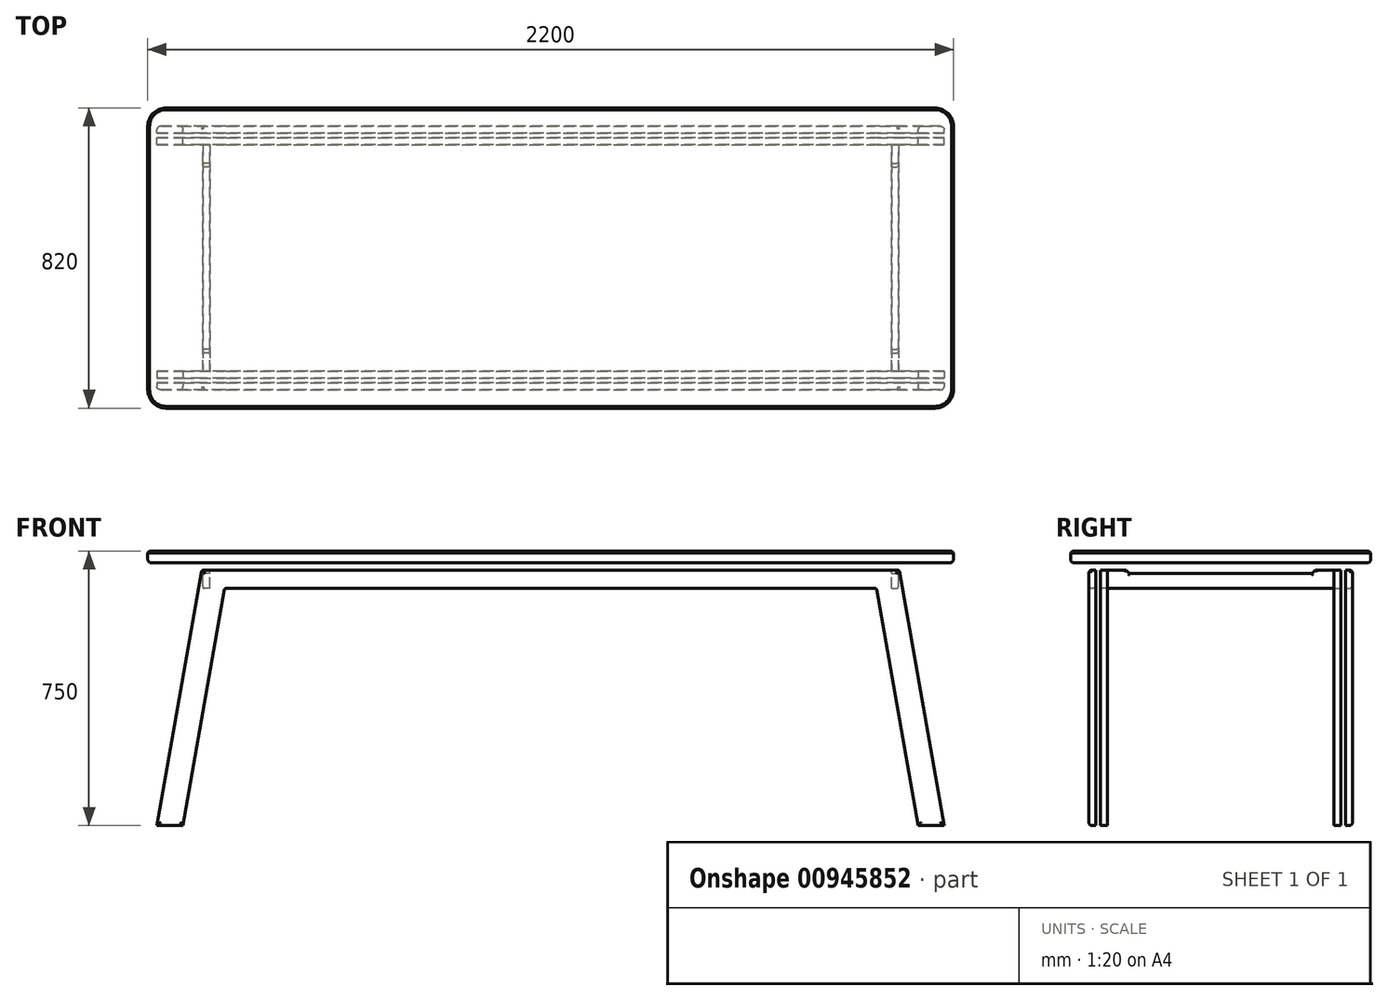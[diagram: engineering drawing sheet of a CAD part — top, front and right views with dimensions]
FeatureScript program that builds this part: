
annotation { "Feature Type Name" : "Feature", "Feature Type Description" : "" }
export const myFeature = defineFeature(function(context is Context, id is Id, definition is map)
    precondition{}
    {
        {
            assignVariable(context, id + "F0", {"name" : "chama", "anyValue" : 5});
        }
        {
            assignVariable(context, id + "F1", {"name" : "fila", "anyValue" : 50});
        }
        {
            assignVariable(context, id + "F2", {"name" : "filb", "anyValue" : 9});
        }
        {
            assignVariable(context, id + "F3", {"name" : "filc", "anyValue" : 5});
        }
        {
            assignVariable(context, id + "F4", {"name" : "w", "anyValue" : 820});
        }
        {
            assignVariable(context, id + "F5", {"name" : "h", "anyValue" : 750});
        }
        {
            assignVariable(context, id + "F6", {"name" : "ld", "anyValue" : 19});
        }
        {
            assignVariable(context, id + "F7", {"name" : "thk", "anyValue" : 32});
        }
        {
            var Q0;
            Q0=qCreatedBy(makeId("Right.planeOp"),FACE);
            cPlane(context, id + "F8", {"entities" : qUnion([Q0]), "cplaneType" : CPlaneType.OFFSET, "offset" : 950 * mm, "width" : 150 * mm, "height" : 150 * mm});
        }
        {
            var Q0;
            Q0=qCreatedBy(makeId("Front.planeOp"),FACE);
            cPlane(context, id + "F9", {"entities" : qUnion([Q0]), "cplaneType" : CPlaneType.OFFSET, "offset" : (getVariable(context, 'w') / 2 - 50) * mm, "width" : 150 * mm, "height" : 150 * mm});
        }
        {
            var Q0;
            Q0=qCreatedBy(makeId("Top.planeOp"),FACE);
            var sketch = newSketch(context, id + "F10", { "sketchPlane" : qUnion([Q0])});
            skLineSegment(sketch, "E0.bottom", {"start": v(1100, -410) * mm, "end": v(-1100, -410) * mm});
            skLineSegment(sketch, "E0.top", {"start": v(1100, 410) * mm, "end": v(-1100, 410) * mm});
            skLineSegment(sketch, "E0.left", {"start": v(1100, -410) * mm, "end": v(1100, 410) * mm});
            skLineSegment(sketch, "E0.right", {"start": v(-1100, -410) * mm, "end": v(-1100, 410) * mm});
            skPoint(sketch, "E0.middle", {"position": v(0, 0) * mm});
            skSolve(sketch);
        }
        {
            var Q0;
            Q0=sQuery(id+"F10.wireOp",EDGE,"E0.top");
            var Q1;
            Q1=sQuery(id+"F10.wireOp",EDGE,"E0.right");
            var Q2;
            Q2=sQuery(id+"F10.wireOp",EDGE,"E0.bottom");
            var Q3;
            Q3=sQuery(id+"F10.wireOp",EDGE,"E0.left");
            extrude(context, id + "F11", {"bodyType" : ToolBodyType.SURFACE, "surfaceEntities" : qUnion([Q0, Q1, Q2, Q3]), "oppositeDirection" : true, "depth" : (getVariable(context, 'h')) * mm, "offsetDistance" : 25.4 * mm});
        }
        {
            var Q0;
            Q0=makeQuery(id+"F10.imprint","IMPRINT",FACE,{"disambiguationData":[TD([[makeQuery(id+"F10.imprint","IMPRINT",EDGE,{"derivedFrom":sQuery(id+"F10.wireOp",EDGE,"E0.bottom")}),-1.0]])]});
            extrude(context, id + "F12", {"entities" : qUnion([Q0]), "oppositeDirection" : true, "depth" : (getVariable(context, 'thk')) * mm, "offsetDistance" : 25.4 * mm});
        }
        {
            var Q0;
            Q0=qCreatedBy(id+"F9.planeOp",FACE);
            var sketch = newSketch(context, id + "F13", { "sketchPlane" : qUnion([Q0])});
            skLineSegment(sketch, "E1", {"start": v(1075, -750) * mm, "end": v(951.92, -52) * mm});
            skLineSegment(sketch, "E2", {"start": v(951.92, -52) * mm, "end": v(-951.92, -52) * mm});
            skLineSegment(sketch, "E3", {"start": v(-951.92, -52) * mm, "end": v(-1075, -750) * mm});
            skLineSegment(sketch, "E4", {"start": v(-1075, -750) * mm, "end": v(-1003.92, -750) * mm});
            skLineSegment(sketch, "E5", {"start": v(-1003.92, -750) * mm, "end": v(-889.66, -102) * mm});
            skLineSegment(sketch, "E6", {"start": v(-889.66, -102) * mm, "end": v(889.66, -102) * mm});
            skLineSegment(sketch, "E7", {"start": v(889.66, -102) * mm, "end": v(1003.92, -750) * mm});
            skLineSegment(sketch, "E8", {"start": v(1003.92, -750) * mm, "end": v(1075, -750) * mm});
            skSolve(sketch);
        }
        {
            var Q0;
            Q0 = qSketchRegion(id + "F13", true);
            extrude(context, id + "F14", {"entities" : qUnion([Q0]), "oppositeDirection" : true, "depth" : (getVariable(context, 'ld')) * mm, "offsetDistance" : 25 * mm});
        }
        {
            var Q0;
            Q0=makeQuery(id+"F12.opExtrude","SWEPT_EDGE",EDGE,{"disambiguationData":[OSD([sQuery(id+"F10.wireOp",EDGE,"E0.bottom"),sQuery(id+"F10.wireOp",EDGE,"E0.left")])]});
            var Q1;
            Q1=makeQuery(id+"F12.opExtrude","SWEPT_EDGE",EDGE,{"disambiguationData":[OSD([sQuery(id+"F10.wireOp",EDGE,"E0.top"),sQuery(id+"F10.wireOp",EDGE,"E0.left")])]});
            var Q2;
            Q2=makeQuery(id+"F12.opExtrude","SWEPT_EDGE",EDGE,{"disambiguationData":[OSD([sQuery(id+"F10.wireOp",EDGE,"E0.top"),sQuery(id+"F10.wireOp",EDGE,"E0.right")])]});
            var Q3;
            Q3=makeQuery(id+"F12.opExtrude","SWEPT_EDGE",EDGE,{"disambiguationData":[OSD([sQuery(id+"F10.wireOp",EDGE,"E0.bottom"),sQuery(id+"F10.wireOp",EDGE,"E0.right")])]});
            fillet(context, id + "F15", {"entities" : qUnion([Q0, Q1, Q2, Q3]), "radius" : (getVariable(context, 'fila')) * mm, "tangentPropagation" : true, "allowEdgeOverflow" : false});
        }
        {
            var Q0;
            Q0=makeQuery(id+"F12.opExtrude","CAP_FACE",FACE,{"disambiguationData":[OSD([sQuery(id+"F10.wireOp",EDGE,"E0.bottom"),sQuery(id+"F10.wireOp",EDGE,"E0.top"),sQuery(id+"F10.wireOp",EDGE,"E0.left"),sQuery(id+"F10.wireOp",EDGE,"E0.right")])],"isStart":false});
            fillet(context, id + "F16", {"entities" : qUnion([Q0]), "radius" : (getVariable(context, 'filb')) * mm, "tangentPropagation" : true, "allowEdgeOverflow" : false});
        }
        {
            var Q0;
            Q0=makeQuery(id+"F12.opExtrude","CAP_FACE",FACE,{"disambiguationData":[OSD([sQuery(id+"F10.wireOp",EDGE,"E0.bottom"),sQuery(id+"F10.wireOp",EDGE,"E0.top"),sQuery(id+"F10.wireOp",EDGE,"E0.left"),sQuery(id+"F10.wireOp",EDGE,"E0.right")])],"isStart":true});
            chamfer(context, id + "F17", {"entities" : qUnion([Q0]), "width" : (getVariable(context, 'chama')) * mm, "tangentPropagation" : true});
        }
        {
            var Q0;
            Q0=makeQuery(id+"F14.opExtrude","SWEPT_EDGE",EDGE,{"disambiguationData":[OSD([sQuery(id+"F13.wireOp",EDGE,"E1"),sQuery(id+"F13.wireOp",EDGE,"E2")])]});
            var Q1;
            Q1=makeQuery(id+"F14.opExtrude","SWEPT_EDGE",EDGE,{"disambiguationData":[OSD([sQuery(id+"F13.wireOp",EDGE,"E2"),sQuery(id+"F13.wireOp",EDGE,"E3")])]});
            var Q2;
            Q2=makeQuery(id+"F14.opExtrude","SWEPT_EDGE",EDGE,{"disambiguationData":[OSD([sQuery(id+"F13.wireOp",EDGE,"E6"),sQuery(id+"F13.wireOp",EDGE,"E7")])]});
            var Q3;
            Q3=makeQuery(id+"F14.opExtrude","SWEPT_EDGE",EDGE,{"disambiguationData":[OSD([sQuery(id+"F13.wireOp",EDGE,"E5"),sQuery(id+"F13.wireOp",EDGE,"E6")])]});
            fillet(context, id + "F18", {"entities" : qUnion([Q0, Q1, Q2, Q3]), "radius" : (getVariable(context, 'filc')) * mm, "tangentPropagation" : true, "allowEdgeOverflow" : false});
        }
        {
            var Q0;
            Q0=makeQuery(id+"F14.opExtrude","SWEPT_BODY",BODY,{"disambiguationData":[OSD([sQuery(id+"F13.wireOp",EDGE,"E1"),sQuery(id+"F13.wireOp",EDGE,"E2"),sQuery(id+"F13.wireOp",EDGE,"E3"),sQuery(id+"F13.wireOp",EDGE,"E4"),sQuery(id+"F13.wireOp",EDGE,"E5"),sQuery(id+"F13.wireOp",EDGE,"E6"),sQuery(id+"F13.wireOp",EDGE,"E7"),sQuery(id+"F13.wireOp",EDGE,"E8")])]});
            transform(context, id + "F19", {"entities" : qUnion([Q0]), "transformType" : TransformType.TRANSLATION_3D, "dx" : 0 * mm, "dy" : (getVariable(context, 'thk')) * mm, "dz" : 0 * mm, "makeCopy" : true});
        }
        {
            var Q0;
            Q0=makeQuery(id+"F14.opExtrude","CAP_FACE",FACE,{"disambiguationData":[OSD([sQuery(id+"F13.wireOp",EDGE,"E1"),sQuery(id+"F13.wireOp",EDGE,"E2"),sQuery(id+"F13.wireOp",EDGE,"E3"),sQuery(id+"F13.wireOp",EDGE,"E4"),sQuery(id+"F13.wireOp",EDGE,"E5"),sQuery(id+"F13.wireOp",EDGE,"E6"),sQuery(id+"F13.wireOp",EDGE,"E7"),sQuery(id+"F13.wireOp",EDGE,"E8")])],"isStart":true});
            fillet(context, id + "F20", {"entities" : qUnion([Q0]), "radius" : (getVariable(context, 'filb')) * mm, "tangentPropagation" : true, "allowEdgeOverflow" : false});
        }
        {
            var Q0;
            Q0=makeQuery(id+"F14.opExtrude","SWEPT_BODY",BODY,{"disambiguationData":[OSD([sQuery(id+"F13.wireOp",EDGE,"E1"),sQuery(id+"F13.wireOp",EDGE,"E2"),sQuery(id+"F13.wireOp",EDGE,"E3"),sQuery(id+"F13.wireOp",EDGE,"E4"),sQuery(id+"F13.wireOp",EDGE,"E5"),sQuery(id+"F13.wireOp",EDGE,"E6"),sQuery(id+"F13.wireOp",EDGE,"E7"),sQuery(id+"F13.wireOp",EDGE,"E8")])]});
            var Q1;
            Q1=makeQuery(id+"F19.opPattern","COPY",BODY,{"derivedFrom":makeQuery(id+"F14.opExtrude","SWEPT_BODY",BODY,{"disambiguationData":[OSD([sQuery(id+"F13.wireOp",EDGE,"E1"),sQuery(id+"F13.wireOp",EDGE,"E2"),sQuery(id+"F13.wireOp",EDGE,"E3"),sQuery(id+"F13.wireOp",EDGE,"E4"),sQuery(id+"F13.wireOp",EDGE,"E5"),sQuery(id+"F13.wireOp",EDGE,"E6"),sQuery(id+"F13.wireOp",EDGE,"E7"),sQuery(id+"F13.wireOp",EDGE,"E8")])]}),"instanceName":"1"});
            var Q2;
            Q2=qCreatedBy(makeId("Front.planeOp"),FACE);
            mirror(context, id + "F21", {"entities" : qUnion([Q0, Q1]), "mirrorPlane" : qUnion([Q2])});
        }
        {
            var Q0;
            Q0=qCreatedBy(id+"F8.planeOp",FACE);
            var sketch = newSketch(context, id + "F22", { "sketchPlane" : qUnion([Q0])});
            skLineSegment(sketch, "E9", {"start": v(-309, -52) * mm, "end": v(309, -52) * mm});
            skLineSegment(sketch, "E10", {"start": v(309, -52) * mm, "end": v(309, -102) * mm});
            skLineSegment(sketch, "E11", {"start": v(309, -102) * mm, "end": v(-309, -102) * mm});
            skLineSegment(sketch, "E12", {"start": v(-309, -102) * mm, "end": v(-309, -52) * mm});
            skLineSegment(sketch, "E13", {"start": v(-259, -52) * mm, "end": v(-249, -62) * mm});
            skLineSegment(sketch, "E14", {"start": v(-249, -62) * mm, "end": v(249, -62) * mm});
            skLineSegment(sketch, "E15", {"start": v(249, -62) * mm, "end": v(259, -52) * mm});
            skSolve(sketch);
        }
        {
            var Q0;
            Q0=makeQuery(id+"F22.imprint","IMPRINT",FACE,{"disambiguationData":[TD([[makeQuery(id+"F22.imprint","IMPRINT",EDGE,{"derivedFrom":sQuery(id+"F22.wireOp",EDGE,"E9")}),-1.0]])]});
            extrude(context, id + "F23", {"entities" : qUnion([Q0]), "oppositeDirection" : true, "depth" : (getVariable(context, 'ld')) * mm, "offsetDistance" : 25 * mm});
        }
        {
            var Q0;
            Q0=makeQuery(id+"F23.opExtrude","CAP_EDGE",EDGE,{"disambiguationData":[OSD([sQuery(id+"F22.wireOp",EDGE,"E9")])],"isStart":true});
            var Q1;
            Q1=makeQuery(id+"F23.opExtrude","CAP_EDGE",EDGE,{"disambiguationData":[OSD([sQuery(id+"F22.wireOp",EDGE,"E11")])],"isStart":true});
            var Q2;
            Q2=makeQuery(id+"F23.opExtrude","CAP_EDGE",EDGE,{"disambiguationData":[OSD([sQuery(id+"F22.wireOp",EDGE,"E13")])],"isStart":true});
            var Q3;
            Q3=makeQuery(id+"F23.opExtrude","CAP_EDGE",EDGE,{"disambiguationData":[OSD([sQuery(id+"F22.wireOp",EDGE,"E14")])],"isStart":true});
            var Q4;
            Q4=makeQuery(id+"F23.opExtrude","CAP_EDGE",EDGE,{"disambiguationData":[OSD([sQuery(id+"F22.wireOp",EDGE,"E15")])],"isStart":true});
            fillet(context, id + "F24", {"entities" : qUnion([Q0, Q1, Q2, Q3, Q4]), "radius" : (getVariable(context, 'filc')) * mm, "tangentPropagation" : true, "allowEdgeOverflow" : false});
        }
        {
            var Q0;
            Q0=makeQuery(id+"F23.opExtrude","SWEPT_BODY",BODY,{"disambiguationData":[OSD([sQuery(id+"F22.wireOp",EDGE,"E9"),sQuery(id+"F22.wireOp",EDGE,"E10"),sQuery(id+"F22.wireOp",EDGE,"E11"),sQuery(id+"F22.wireOp",EDGE,"E12"),sQuery(id+"F22.wireOp",EDGE,"E13"),sQuery(id+"F22.wireOp",EDGE,"E14"),sQuery(id+"F22.wireOp",EDGE,"E15")])]});
            var Q1;
            Q1=qCreatedBy(makeId("Right.planeOp"),FACE);
            mirror(context, id + "F25", {"entities" : qUnion([Q0]), "mirrorPlane" : qUnion([Q1])});
        }
    });
